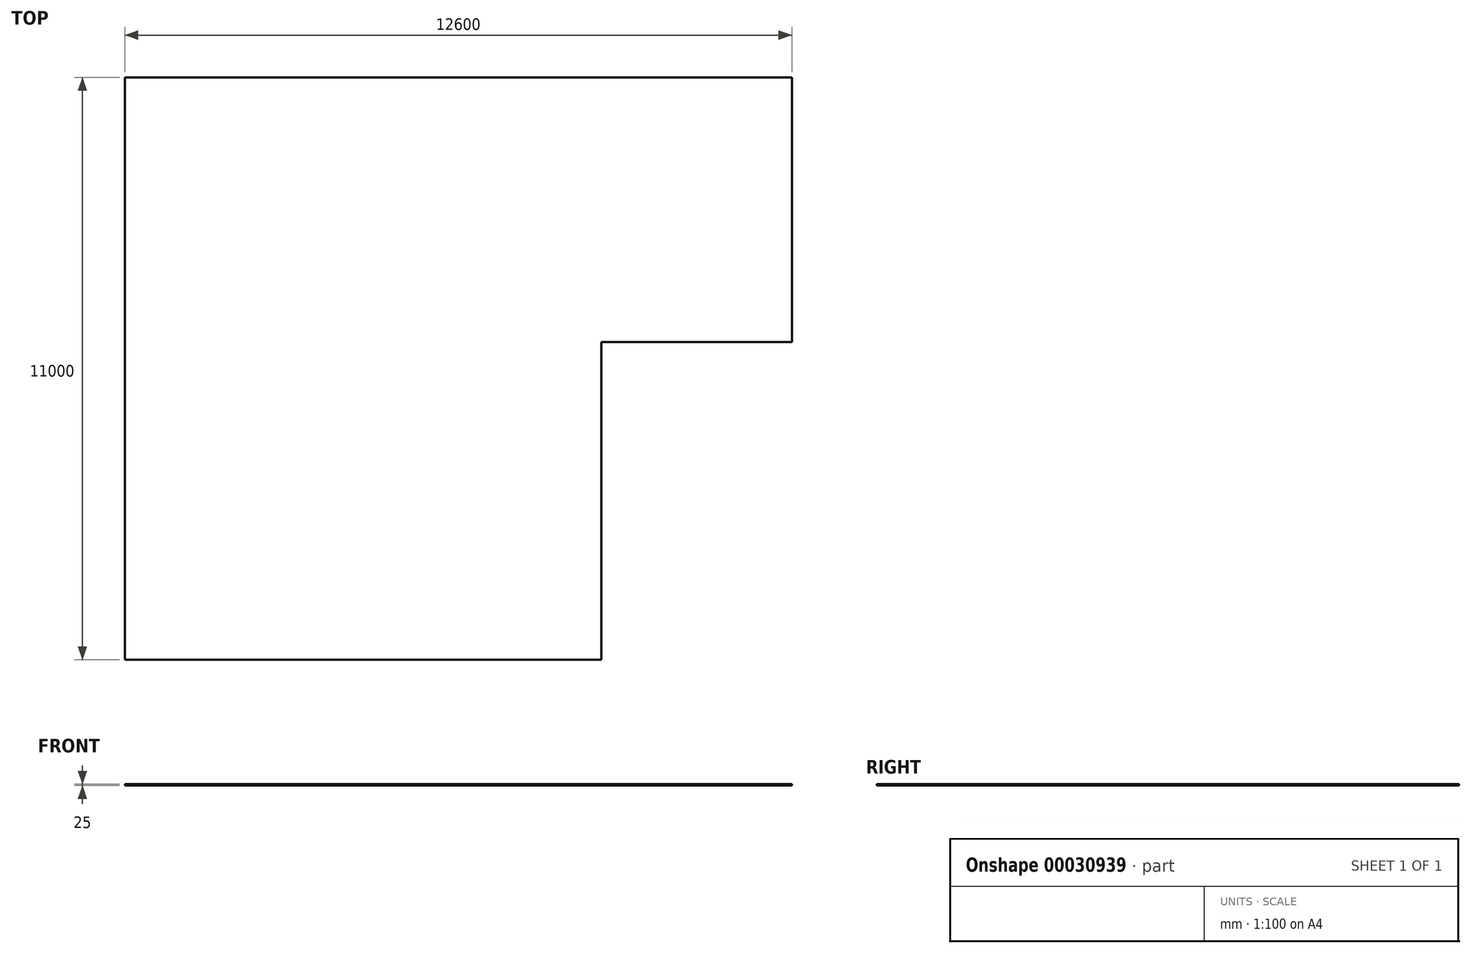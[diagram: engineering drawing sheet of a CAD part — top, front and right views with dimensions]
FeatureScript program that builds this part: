
annotation { "Feature Type Name" : "Feature", "Feature Type Description" : "" }
export const myFeature = defineFeature(function(context is Context, id is Id, definition is map)
    precondition{}
    {
        {
            var Q0;
            Q0=qCreatedBy(makeId("Top.planeOp"),FACE);
            var sketch = newSketch(context, id + "F0", { "sketchPlane" : qUnion([Q0])});
            skLineSegment(sketch, "E0", {"start": v(0, 0) * mm, "end": v(9000, 0) * mm});
            skLineSegment(sketch, "E1", {"start": v(9000, 0) * mm, "end": v(9000, 6000) * mm});
            skLineSegment(sketch, "E2", {"start": v(9000, 6000) * mm, "end": v(12600, 6000) * mm});
            skLineSegment(sketch, "E3", {"start": v(12600, 6000) * mm, "end": v(12600, 11000) * mm});
            skLineSegment(sketch, "E4", {"start": v(12600, 11000) * mm, "end": v(0, 11000) * mm});
            skLineSegment(sketch, "E5", {"start": v(0, 11000) * mm, "end": v(0, 0) * mm});
            skSolve(sketch);
        }
        {
            var Q0;
            Q0 = qSketchRegion(id + "F0", true);
            extrude(context, id + "F1", {"entities" : qUnion([Q0]), "depth" : 25 * mm});
        }
    });
